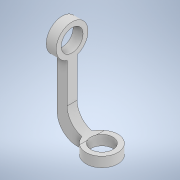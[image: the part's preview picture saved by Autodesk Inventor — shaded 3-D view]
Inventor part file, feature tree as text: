
AUTODESK INVENTOR PART (.ipt)
format: ipt  version: 2022 (Build 260153000, 153)  size: 160,768 bytes
history: native  units: mm
features: extrude x6, sketch x6, other x1, fillet x1
ambient origin geometry x8: Origin, YZ Plane, XZ Plane, XY Plane, X Axis, Y Axis, Z Axis, Center Point
bodies: Body1 (feature_tree)
feature tree (14):
  other  "Bryła1"
  extrude  "Wyciągnięcie proste1"  Depth=22.0mm
  extrude  "Wyciągnięcie proste2"  Depth=5.0mm
  fillet  "Zaokrąglenie1"  Radius=10.0mm
  extrude  "Wyciągnięcie proste3"  Depth=84.8mm
  extrude  "Wyciągnięcie proste4"  Depth=30.0mm
  extrude  "Wyciągnięcie proste5"  Depth=10.0mm
  extrude  "Wyciągnięcie proste6"  Depth=10.0mm
  sketch  "Szkic2"
  sketch  "Szkic4"
  sketch  "Szkic7"
  sketch  "Szkic8"
  sketch  "Szkic9"
  sketch  "Szkic10"
